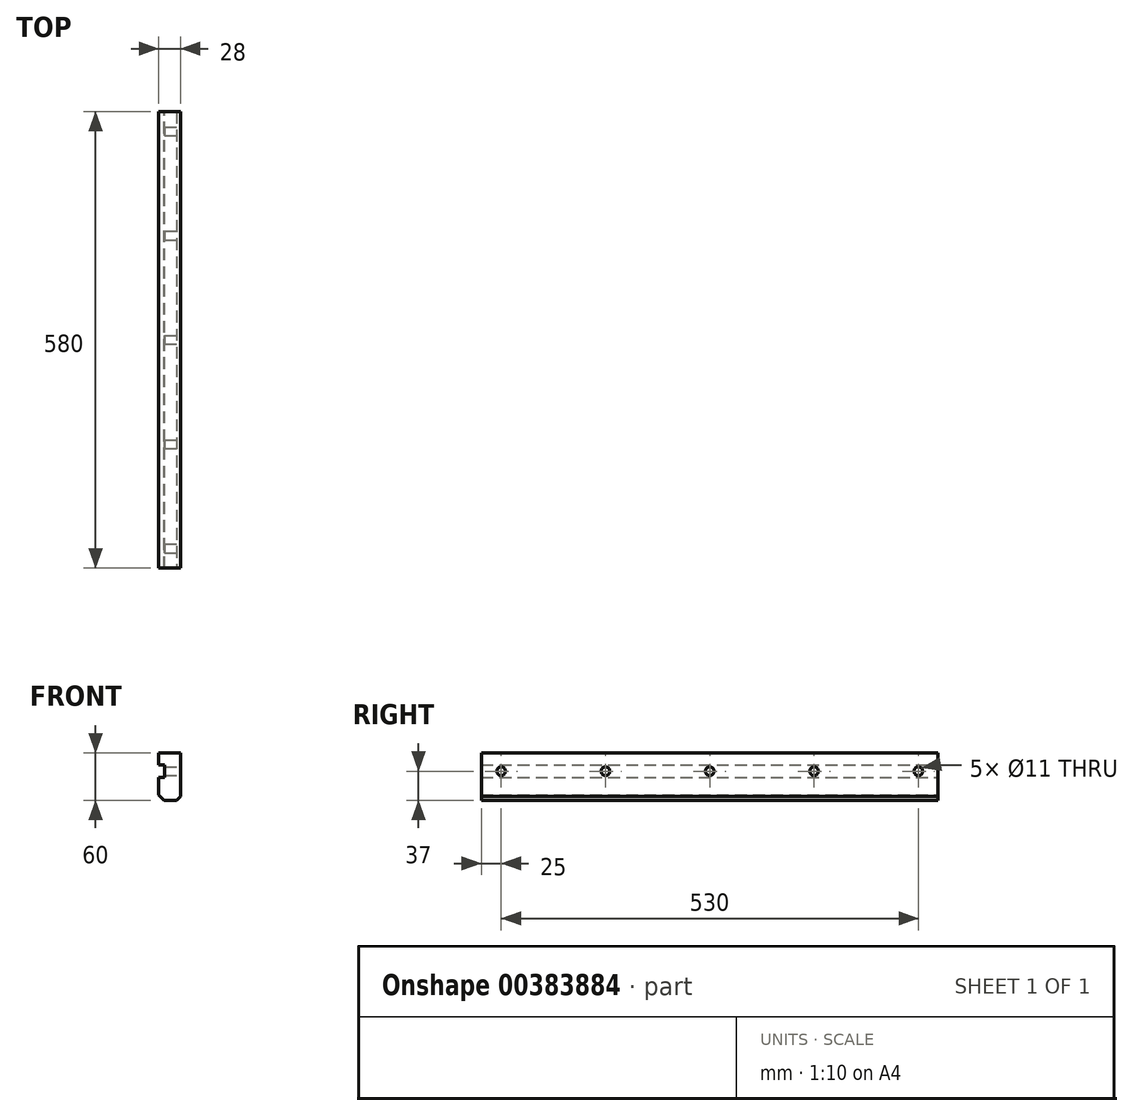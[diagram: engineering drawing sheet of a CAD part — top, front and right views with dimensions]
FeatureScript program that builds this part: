
annotation { "Feature Type Name" : "Feature", "Feature Type Description" : "" }
export const myFeature = defineFeature(function(context is Context, id is Id, definition is map)
    precondition{}
    {
        {
            var Q0;
            Q0=qCreatedBy(makeId("Front.planeOp"),FACE);
            var sketch = newSketch(context, id + "F0", { "sketchPlane" : qUnion([Q0])});
            skLineSegment(sketch, "E0.bottom", {"start": v(0, 0) * mm, "end": v(28, 0) * mm});
            skLineSegment(sketch, "E0.top", {"start": v(0, -60) * mm, "end": v(28, -60) * mm});
            skLineSegment(sketch, "E0.left", {"start": v(0, 0) * mm, "end": v(0, -60) * mm});
            skLineSegment(sketch, "E0.right", {"start": v(28, 0) * mm, "end": v(28, -60) * mm});
            skLineSegment(sketch, "E1", {"start": v(0, -15) * mm, "end": v(8, -15) * mm});
            skLineSegment(sketch, "E2", {"start": v(8, -15) * mm, "end": v(8, -31) * mm});
            skLineSegment(sketch, "E3", {"start": v(8, -31) * mm, "end": v(0, -31) * mm});
            skLineSegment(sketch, "E4", {"start": v(0, -52.93) * mm, "end": v(7.07, -60) * mm});
            skSolve(sketch);
        }
        {
            var Q0;
            {var subQ1=sQuery(id+"F0.wireOp",EDGE,"E0.bottom");Q0=makeQuery(id+"F0.imprint","IMPRINT",FACE,{"disambiguationData":[TD([[makeQuery(id+"F0.imprint","IMPRINT",EDGE,{"derivedFrom":subQ1}),-1.0]])]});}
            extrude(context, id + "F1", {"entities" : qUnion([Q0]), "depth" : 580 * mm});
        }
        {
            var Q0;
            Q0=makeQuery(id+"F1.opExtrude","SWEPT_FACE",FACE,{"disambiguationData":[OSD([sQuery(id+"F0.wireOp",EDGE,"E0.right")])]});
            var sketch = newSketch(context, id + "F2", { "sketchPlane" : qUnion([Q0])});
            skLineSegment(sketch, "E5.0", {"start": v(-580, 0) * mm, "end": v(-580, -60) * mm});
            skLineSegment(sketch, "E6.0", {"start": v(0, 0) * mm, "end": v(0, -60) * mm});
            skLineSegment(sketch, "E7.0", {"start": v(-580, 0) * mm, "end": v(0, 0) * mm});
            skLineSegment(sketch, "E8.0", {"start": v(-580, -60) * mm, "end": v(0, -60) * mm});
            skLineSegment(sketch, "E9", {"start": v(-580, -23) * mm, "end": v(0, -23) * mm, "construction": true});
            skCircle(sketch, "E10", {"center": v(-555, -23) * mm, "radius": 5 * mm});
            skCircle(sketch, "E11", {"center": v(-422.5, -23) * mm, "radius": 5 * mm});
            skCircle(sketch, "E12", {"center": v(-290, -23) * mm, "radius": 5 * mm});
            skCircle(sketch, "E13", {"center": v(-157.5, -23) * mm, "radius": 5 * mm});
            skCircle(sketch, "E14", {"center": v(-25, -23) * mm, "radius": 5 * mm});
            skSolve(sketch);
        }
        {
            var Q0;
            Q0=sQuery(id+"F2.wireOp",VERTEX,"E10.center");
            var Q1;
            Q1=sQuery(id+"F2.wireOp",VERTEX,"E11.center");
            var Q2;
            Q2=sQuery(id+"F2.wireOp",VERTEX,"E12.center");
            var Q3;
            Q3=sQuery(id+"F2.wireOp",VERTEX,"E13.center");
            var Q4;
            Q4=sQuery(id+"F2.wireOp",VERTEX,"E14.center");
            var Q5;
            Q5=makeQuery(id+"F1.opExtrude","SWEPT_BODY",BODY,{"disambiguationData":[OSD([sQuery(id+"F0.wireOp",EDGE,"E0.bottom"),sQuery(id+"F0.wireOp",EDGE,"E0.top"),sQuery(id+"F0.wireOp",EDGE,"E0.left"),sQuery(id+"F0.wireOp",EDGE,"E0.right"),sQuery(id+"F0.wireOp",EDGE,"E1"),sQuery(id+"F0.wireOp",EDGE,"E2"),sQuery(id+"F0.wireOp",EDGE,"E3"),sQuery(id+"F0.wireOp",EDGE,"E4")])]});
            hole(context, id + "F3", {"style" : HoleStyle.SIMPLE, "endStyle" : HoleEndStyle.THROUGH, "standardTappedOrClearance" : lookupTablePath({ "standard" : "ISO", "fit" : "Normal", "size" : "M10", "type" : "Clearance" }), "standardBlindInLast" : lookupTablePath({ "fit" : "Standard", "standard" : "ISO", "size" : "M10", "type" : "Clearance" }), "holeDiameter" : 11 * mm, "isTappedThrough" : true, "tappedDepth" : 12 * mm, "tapClearance" : 3, "locations" : qUnion([Q0, Q1, Q2, Q3, Q4]), "scope" : qUnion([Q5])});
        }
        {
            var Q0;
            Q0=makeQuery(id+"F1.opExtrude","SWEPT_EDGE",EDGE,{"disambiguationData":[OSD([sQuery(id+"F0.wireOp",EDGE,"E0.top"),sQuery(id+"F0.wireOp",EDGE,"E0.right")])]});
            chamfer(context, id + "F4", {"entities" : qUnion([Q0]), "width" : 5 * mm, "tangentPropagation" : true});
        }
    });
